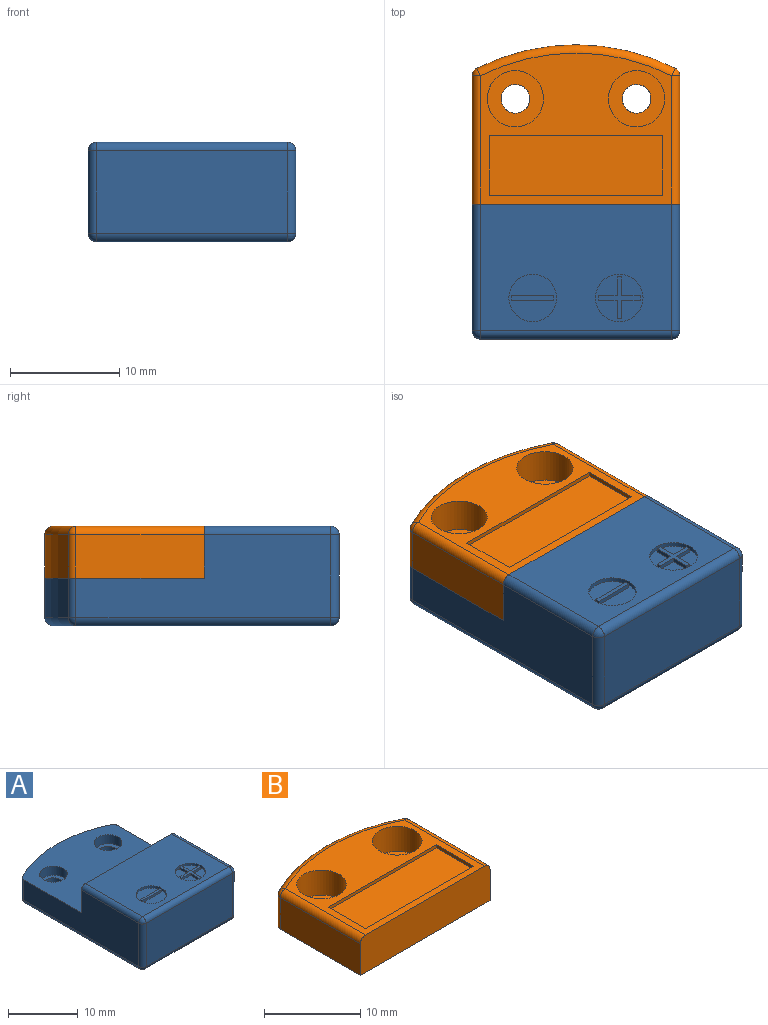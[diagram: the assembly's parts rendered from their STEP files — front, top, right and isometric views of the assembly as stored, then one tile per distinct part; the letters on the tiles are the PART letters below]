
ASSEMBLY  parts=2 mates=1
PART A: 53 faces, bbox 19.7x28.7x9.1 mm
  f0: plane 17.53x11.62mm, normal (0,0,1), area 173.7mm2, adj f9,f25,f32,f47,f48,f52
  f1: plane 19.05x14.61mm, normal (0,0,1), area 238.7mm2, adj f4,f5,f6,f9,f10,f12,f36,f37
  f2: cylinder r=1.32mm len=2.78mm, axis (0,0,-1), area 23.1mm2, adj f8,f13
  f3: cylinder r=1.32mm len=2.78mm, axis (0,0,-1), area 23.1mm2, adj f8,f11
  f4: plane 23.38x7.6mm, normal (1,0,0), area 130.7mm2, adj f1,f9,f37,f42,f48,f49
  f5: cylinder r=20.24mm len=18.21mm, axis (0,0,-1), area 68.1mm2, adj f1,f36,f37,f38
  f6: plane 23.38x7.6mm, normal (-1,0,0), area 130.7mm2, adj f1,f9,f36,f41,f46,f47
  f7: plane 17.53x7.6mm, normal (0,-1,0), area 133.3mm2, adj f43,f46,f49,f52
  f8: plane 25.46x17.53mm, normal (0,0,-1), area 423.4mm2, adj f2,f3,f38,f41,f42,f43
  f9: plane 19.05x4.76mm, normal (0,1,0), area 90.5mm2, adj f0,f1,f4,f6,f47,f48
  f10: cylinder r=1.98mm len=3.97mm, axis (0,0,1), area 19.8mm2, adj f1,f11
  f11: plane 3.97x3.97mm, normal (0,0,1), area 6.9mm2, adj f3,f10
  f12: cylinder r=1.98mm len=3.97mm, axis (0,0,1), area 19.8mm2, adj f1,f13
  f13: plane 3.97x3.97mm, normal (0,0,1), area 6.9mm2, adj f2,f12
  f14: plane 0.4x0.4mm, normal (0,1,0), area 0.2mm2, adj f15,f26,f27,f35
  f15: plane 1.73x0.4mm, normal (1,0,0), area 0.7mm2, adj f14,f16,f27,f35
  f16: plane 1.73x0.4mm, normal (0,1,0), area 0.7mm2, adj f15,f17,f27,f35
  f17: plane 0.4x0.4mm, normal (1,0,0), area 0.2mm2, adj f16,f18,f27,f35
  f18: plane 1.73x0.4mm, normal (0,-1,0), area 0.7mm2, adj f17,f19,f27,f35
  f19: plane 1.73x0.4mm, normal (1,0,0), area 0.7mm2, adj f18,f20,f27,f35
  f20: plane 0.4x0.4mm, normal (0,-1,0), area 0.2mm2, adj f19,f21,f27,f35
  f21: plane 1.73x0.4mm, normal (-1,0,0), area 0.7mm2, adj f20,f22,f27,f35
  f22: plane 1.73x0.4mm, normal (0,-1,0), area 0.7mm2, adj f21,f23,f27,f35
  f23: plane 0.4x0.4mm, normal (-1,0,0), area 0.2mm2, adj f22,f24,f27,f35
  f24: plane 1.73x0.4mm, normal (0,1,0), area 0.7mm2, adj f23,f26,f27,f35
  f25: cylinder r=2.18mm len=4.37mm, axis (0,0,1), area 5.4mm2, adj f0,f27
  f26: plane 1.73x0.4mm, normal (-1,0,0), area 0.7mm2, adj f14,f24,f27,f35
  f27: plane 4.37x4.37mm, normal (0,0,1), area 12.1mm2, adj f14,f15,f16,f17,f18,f19,f20,f21
  f28: plane 0.4x0.4mm, normal (1,0,0), area 0.2mm2, adj f29,f31,f33,f34
  f29: plane 3.86x0.4mm, normal (0,-1,0), area 1.5mm2, adj f28,f30,f33,f34
  f30: plane 0.4x0.4mm, normal (-1,0,0), area 0.2mm2, adj f29,f31,f33,f34
  f31: plane 3.86x0.4mm, normal (0,1,0), area 1.5mm2, adj f28,f30,f33,f34
  f32: cylinder r=2.18mm len=4.37mm, axis (0,0,1), area 5.4mm2, adj f0,f33
  f33: plane 4.37x4.37mm, normal (0,0,1), area 13.4mm2, adj f28,f29,f30,f31,f32
  f34: plane 3.86x0.4mm, normal (0,0,1), area 1.5mm2, adj f28,f29,f30,f31
  f35: plane 3.86x3.86mm, normal (0,0,1), area 2.9mm2, adj f14,f15,f16,f17,f18,f19,f20,f21
  f36: cylinder r=0.76mm len=3.6mm, axis (0,0,-1), area 3mm2, adj f1,f5,f6,f39
  f37: cylinder r=0.76mm len=3.6mm, axis (0,0,-1), area 3mm2, adj f1,f4,f5,f40
  f38: torus R=19.48mm, axis (0,0,1), area 22.3mm2, adj f5,f8,f39,f40
  f39: sphere r=0.76mm, area 0.6mm2, adj f36,f38,f41
  f40: sphere r=0.76mm, area 0.6mm2, adj f37,f38,f42
  f41: cylinder r=0.76mm len=23.38mm, axis (0,-1,0), area 28mm2, adj f6,f8,f39,f44
  f42: cylinder r=0.76mm len=23.38mm, axis (0,1,0), area 28mm2, adj f4,f8,f40,f45
  f43: cylinder r=0.76mm len=17.53mm, axis (1,0,0), area 21mm2, adj f7,f8,f44,f45
  f44: sphere r=0.76mm, area 0.9mm2, adj f41,f43,f46
  f45: sphere r=0.76mm, area 0.9mm2, adj f42,f43,f49
  f46: cylinder r=0.76mm len=7.6mm, axis (0,0,-1), area 9.1mm2, adj f6,f7,f44,f50
  f47: cylinder r=0.76mm len=11.62mm, axis (0,1,0), area 13.9mm2, adj f0,f6,f9,f50
  f48: cylinder r=0.76mm len=11.62mm, axis (0,-1,0), area 13.9mm2, adj f0,f4,f9,f51
  f49: cylinder r=0.76mm len=7.6mm, axis (0,0,1), area 9.1mm2, adj f4,f7,f45,f51
  f50: sphere r=0.76mm, area 0.9mm2, adj f46,f47,f52
  f51: sphere r=0.76mm, area 0.9mm2, adj f48,f49,f52
  f52: cylinder r=0.76mm len=17.53mm, axis (-1,0,0), area 21mm2, adj f0,f7,f50,f51
PART B: 24 faces, bbox 19.7x16.3x4.8 mm
  f0: plane 17.53x13.84mm, normal (0,0,1), area 101.7mm2, adj f3,f8,f10,f12,f13,f14,f15,f18
  f1: cylinder r=1.32mm len=2.64mm, axis (0,0,-1), area 13.2mm2, adj f7,f11
  f2: cylinder r=1.32mm len=2.64mm, axis (0,0,-1), area 13.2mm2, adj f7,f9
  f3: plane 19.05x4.76mm, normal (0,-1,0), area 90.5mm2, adj f0,f4,f6,f7,f18,f23
  f4: plane 11.76x4mm, normal (1,0,0), area 47mm2, adj f3,f7,f17,f18
  f5: cylinder r=20.24mm len=18.21mm, axis (0,0,-1), area 75.6mm2, adj f7,f17,f20,f21
  f6: plane 11.76x4mm, normal (-1,0,0), area 47mm2, adj f3,f7,f20,f23
  f7: plane 19.05x14.61mm, normal (0,0,-1), area 252.4mm2, adj f1,f2,f3,f4,f5,f6,f17,f20
  f8: cylinder r=2.58mm len=5.16mm, axis (0,0,1), area 51.5mm2, adj f0,f9
  f9: plane 5.16x5.16mm, normal (0,0,1), area 15.4mm2, adj f2,f8
  f10: cylinder r=2.58mm len=5.16mm, axis (0,0,1), area 51.5mm2, adj f0,f11
  f11: plane 5.16x5.16mm, normal (0,0,1), area 15.4mm2, adj f1,f10
  f12: plane 5.49x0.4mm, normal (1,0,0), area 2.2mm2, adj f0,f13,f15,f16
  f13: plane 15.88x0.4mm, normal (0,1,0), area 6.3mm2, adj f0,f12,f14,f16
  f14: plane 5.49x0.4mm, normal (-1,0,0), area 2.2mm2, adj f0,f13,f15,f16
  f15: plane 15.88x0.4mm, normal (0,-1,0), area 6.3mm2, adj f0,f12,f14,f16
  f16: plane 15.88x5.49mm, normal (0,0,1), area 87.2mm2, adj f12,f13,f14,f15
  f17: cylinder r=0.76mm len=4mm, axis (0,0,-1), area 3.4mm2, adj f4,f5,f7,f19
  f18: cylinder r=0.76mm len=11.76mm, axis (0,-1,0), area 14.1mm2, adj f0,f3,f4,f19
  f19: sphere r=0.76mm, area 0.6mm2, adj f17,f18,f21
  f20: cylinder r=0.76mm len=4mm, axis (0,0,-1), area 3.4mm2, adj f5,f6,f7,f22
  f21: torus R=19.48mm, axis (0,0,1), area 22.3mm2, adj f0,f5,f19,f22
  f22: sphere r=0.76mm, area 0.6mm2, adj f20,f21,f23
  f23: cylinder r=0.76mm len=11.76mm, axis (0,1,0), area 14.1mm2, adj f0,f3,f6,f22
PLACE A t=(-54.63,16.75,6.64)mm
PLACE B t=(-54.63,16.75,6.64)mm
MATE fastened A.f9 <-> B.f3  axis (0,1,0) through (15.22,13.32,13.38)mm
